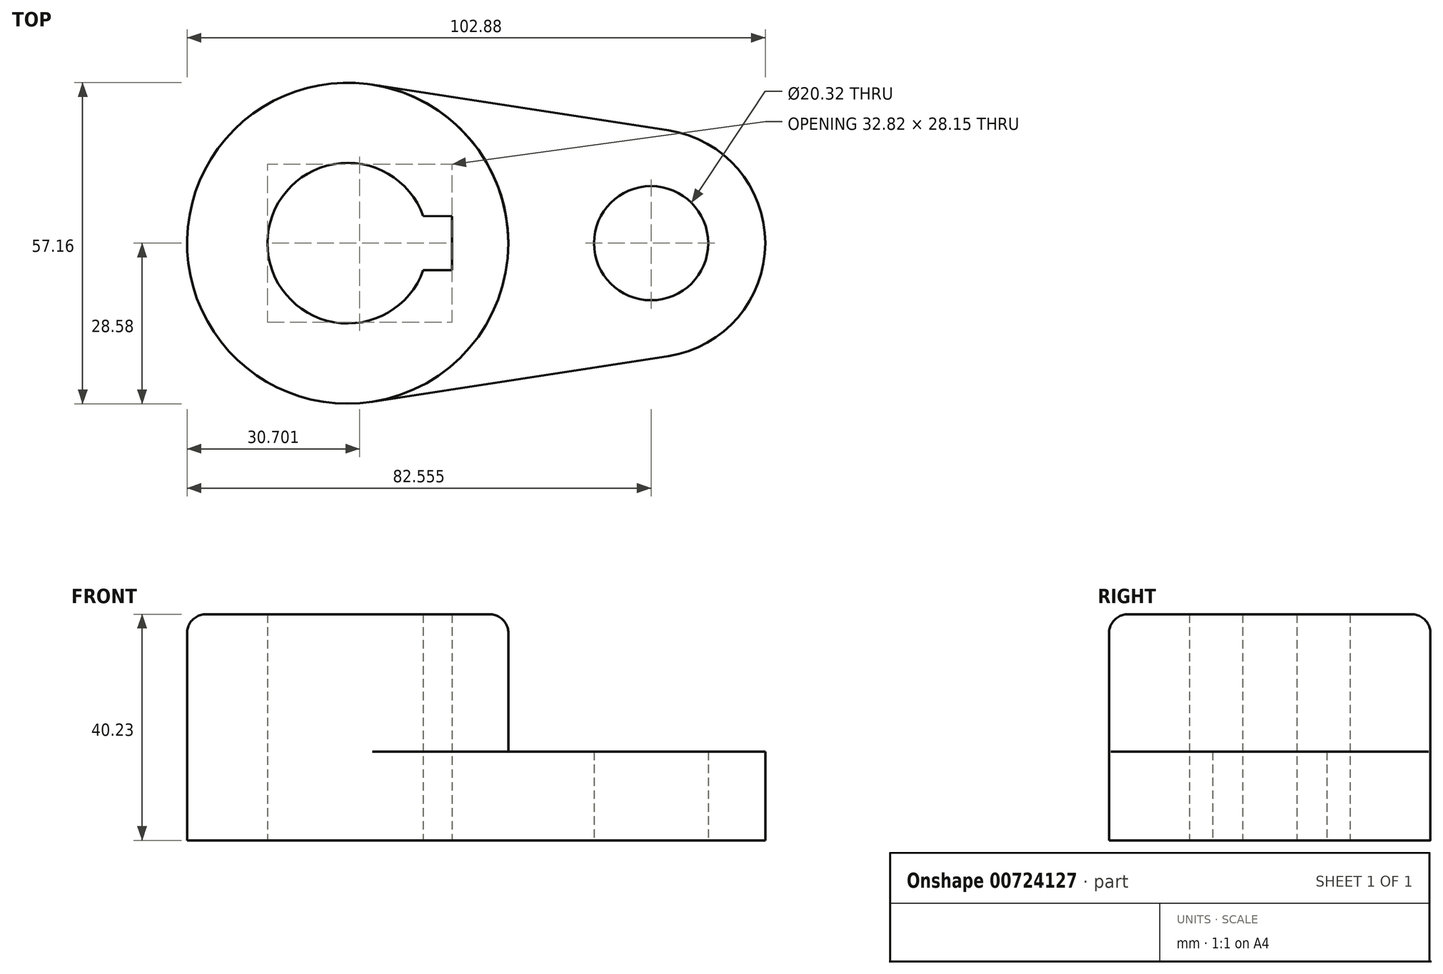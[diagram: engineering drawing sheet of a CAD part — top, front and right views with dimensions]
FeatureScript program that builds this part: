
annotation { "Feature Type Name" : "Feature", "Feature Type Description" : "" }
export const myFeature = defineFeature(function(context is Context, id is Id, definition is map)
    precondition{}
    {
        {
            var Q0;
            Q0=qCreatedBy(makeId("Top.planeOp"),FACE);
            var sketch = newSketch(context, id + "F0", { "sketchPlane" : qUnion([Q0])});
            skArc(sketch, "E0", {"start": v(13.45, 4.83) * mm, "mid": v(-14.29, 0) * mm, "end": v(13.45, -4.83) * mm});
            skCircle(sketch, "E1", {"center": v(0, 0) * mm, "radius": 28.58 * mm});
            skLineSegment(sketch, "E2", {"start": v(0, 0) * mm, "end": v(53.98, 0) * mm});
            skPoint(sketch, "E3", {"position": v(13.45, 4.83) * mm});
            skPoint(sketch, "E4", {"position": v(13.45, -4.83) * mm});
            skPoint(sketch, "E5", {"position": v(18.53, -4.8) * mm});
            skPoint(sketch, "E6", {"position": v(18.53, 4.8) * mm});
            skLineSegment(sketch, "E7", {"start": v(18.53, 4.8) * mm, "end": v(18.53, -4.8) * mm});
            skLineSegment(sketch, "E8", {"start": v(13.45, -4.83) * mm, "end": v(18.53, -4.8) * mm});
            skLineSegment(sketch, "E9", {"start": v(18.53, 4.8) * mm, "end": v(13.45, 4.83) * mm});
            skCircle(sketch, "E10", {"center": v(53.98, 0) * mm, "radius": 10.16 * mm});
            skCircle(sketch, "E11", {"center": v(53.98, 0) * mm, "radius": 20.32 * mm});
            skLineSegment(sketch, "E12", {"start": v(4.37, 28.24) * mm, "end": v(57.08, 20.08) * mm});
            skLineSegment(sketch, "E13", {"start": v(4.37, -28.24) * mm, "end": v(57.08, -20.08) * mm});
            skSolve(sketch);
        }
        {
            var Q0;
            {var subQ0=sQuery(id+"F0.wireOp",EDGE,"E12");Q0=makeQuery(id+"F0.imprint","IMPRINT",FACE,{"disambiguationData":[TD([[makeQuery(id+"F0.imprint","IMPRINT",EDGE,{"derivedFrom":subQ0}),-1.0]])]});}
            var Q1;
            {var subQ0=sQuery(id+"F0.wireOp",EDGE,"E13");Q1=makeQuery(id+"F0.imprint","IMPRINT",FACE,{"disambiguationData":[TD([[makeQuery(id+"F0.imprint","IMPRINT",EDGE,{"derivedFrom":subQ0}),1.0]])]});}
            var Q2;
            Q2=makeQuery(id+"F0.imprint","IMPRINT",FACE,{"disambiguationData":[TD([[makeQuery(id+"F0.imprint","IMPRINT",EDGE,{"derivedFrom":sQuery(id+"F0.wireOp",EDGE,"E10")}),-1.0]])]});
            extrude(context, id + "F1", {"entities" : qUnion([Q0, Q1, Q2]), "depth" : 15.77 * mm, "offsetDistance" : 25.4 * mm});
        }
        {
            var Q0;
            Q0=makeQuery(id+"F0.imprint","IMPRINT",FACE,{"disambiguationData":[TD([[makeQuery(id+"F0.imprint","IMPRINT",EDGE,{"derivedFrom":sQuery(id+"F0.wireOp",EDGE,"E0")}),-1.0]])]});
            extrude(context, id + "F2", {"entities" : qUnion([Q0]), "operationType" : NewBodyOperationType.ADD, "depth" : 40.23 * mm, "offsetDistance" : 25.4 * mm});
        }
        {
            var Q0;
            Q0=makeQuery(id+"F2.opExtrude","CAP_EDGE",EDGE,{"disambiguationData":[OSD([sQuery(id+"F0.wireOp",EDGE,"E1")])],"isStart":false});
            fillet(context, id + "F3", {"entities" : qUnion([Q0]), "radius" : 3.3 * mm, "tangentPropagation" : true, "allowEdgeOverflow" : false});
        }
    });
